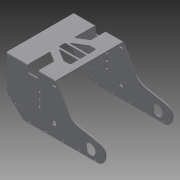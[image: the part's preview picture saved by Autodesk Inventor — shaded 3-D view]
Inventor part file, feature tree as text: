
AUTODESK INVENTOR PART (.ipt)
format: ipt  version: 2015 (Build 190159000, 159)  size: 620,032 bytes
history: native  units: mm
features: sketch x4, extrude x3, other x3, fillet x2
ambient origin geometry x8: Origin, YZ Plane, XZ Plane, XY Plane, X Axis, Y Axis, Z Axis, Center Point
bodies: Body1 (feature_tree)
feature tree (12):
  extrude  "Extrusion22"  Depth=180.0mm
  extrude  "Extrusion23"  Depth=50.0mm
  extrude  "Extrusion24"  Depth=25.0mm
  fillet  "Fillet15"  Radius=5.0mm
  fillet  "Fillet16"  Radius=5.0mm
  other  "Bend Part35"
  other  "Bend Part36"
  other  "Profile"
  sketch  "Sketch40"  dims[d1=80.0mm d8=180.0mm]
  sketch  "Sketch41"  dims[d9=20.0mm d11=50.0mm]
  sketch  "Sketch42"  dims[d14=50.0mm d15=25.0mm d17=5.0mm d19=5.0mm d21=30.0mm]
  sketch  "Sketch43"  dims[d25=73.0mm d127=97.0mm d150=5.0mm d151=5.0mm d152=50.0mm d162=5.0mm d163=5.0mm d182=10.0mm d183=6.0mm d184=10.0mm d220=20.0mm d221=5.0mm d222=5.0mm d223=50.0mm d224=50.0mm d240=20.0mm d248=40.0mm d285=47.0mm d294=25.0mm d324=5.0mm d326=25.0mm d329=25.0mm d344=6.0mm d358=6.0mm d397=10.0mm d398=10.0mm d404=5.0mm d406=45.0mm d445=20.0mm d446=30.0mm d448=45.0deg d460=5.606189mm d463=30.0deg d467=42.0mm d468=36.0mm d469=150.0deg d483=12.0mm d486=42.0mm d487=150.0deg d488=36.0mm d489=150.0deg d501=6.0mm d505=150.0mm d517=3.0mm d518=3.0mm d519=3.0mm d520=3.0mm d521=9.5mm d522=25.0mm d528=20.0mm d530=65.0mm d533=20.0mm d553=50.0mm d555=10.0mm d567=25.923375mm d568=5.0mm d570=10.0mm d571=2.0mm d581=65.0mm d586=25.0mm d587=300.0mm d593=218.0mm d594=38.0mm d595=12.0mm d596=3.0mm d597=47.0mm d599=13.0mm d600=143.0mm d601=12.0mm d602=89.0mm d603=1.0mm d608=3.0mm d609=54.0mm d610=3.0mm d611=233.0mm d612=18.5mm d613=18.5mm d614=1.0mm d615=3.0mm d616=0.0mm d617=239.0mm d618=30.0mm d619=25.0mm d620=15.0mm d621=25.0mm d622=15.0mm d623=30.0mm d624=3.0mm d625=18.0mm d626=3.0mm d627=18.0mm d628=10.0mm d629=0.0mm d630=20.0mm d631=53.0mm d633=85.0mm d634=120.0mm d635=10.0mm d636=0.0mm d637=5.0mm d638=2.0mm d639=1.0mm d640=90.0deg d641=1.0mm d642=90.0deg]
